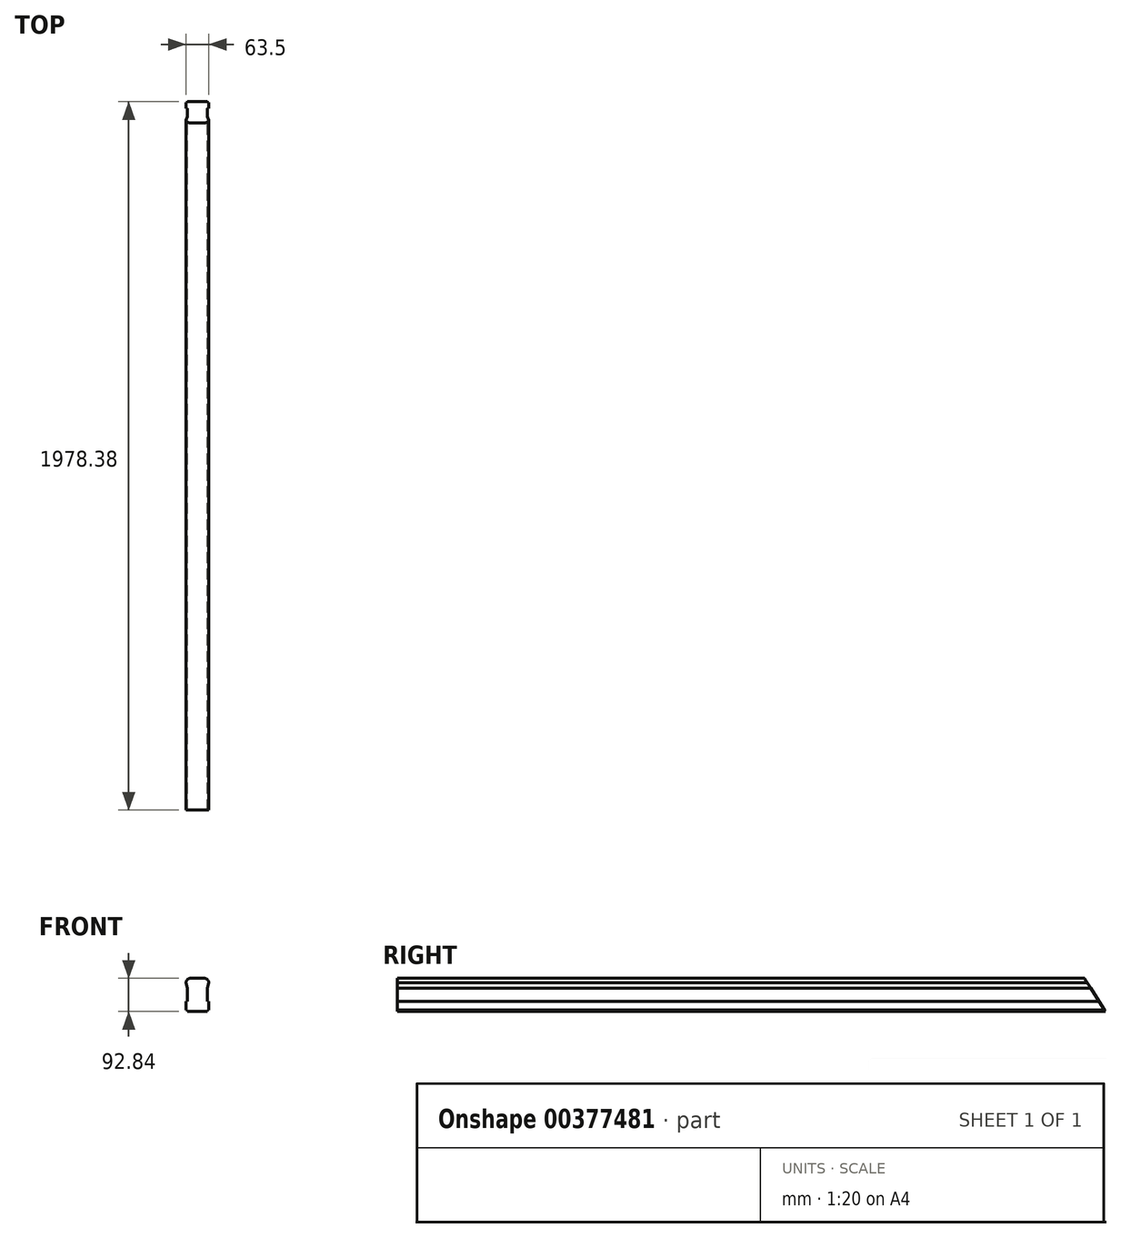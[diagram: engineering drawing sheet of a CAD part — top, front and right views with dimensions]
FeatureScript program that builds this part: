
annotation { "Feature Type Name" : "Feature", "Feature Type Description" : "" }
export const myFeature = defineFeature(function(context is Context, id is Id, definition is map)
    precondition{}
    {
        {
            var Q0;
            Q0=qCreatedBy(makeId("Front.planeOp"),FACE);
            var sketch = newSketch(context, id + "F0", { "sketchPlane" : qUnion([Q0])});
            skLineSegment(sketch, "E0.bottom", {"start": v(-19.05, 44.45) * mm, "end": v(19.05, 44.45) * mm});
            skLineSegment(sketch, "E0.top", {"start": v(-31.75, -44.45) * mm, "end": v(-27.75, -44.45) * mm});
            skLineSegment(sketch, "E0.left", {"start": v(-31.75, -20.19) * mm, "end": v(-31.75, -44.45) * mm});
            skLineSegment(sketch, "E0.right", {"start": v(31.75, -20.19) * mm, "end": v(31.75, -44.45) * mm});
            skPoint(sketch, "E0.middle", {"position": v(0, 0) * mm});
            skPoint(sketch, "E1.visualSharp", {"position": v(-31.75, 44.45) * mm});
            skArc(sketch, "E1.filletArc", {"start": v(-19.05, 44.45) * mm, "mid": v(-28.03, 40.73) * mm, "end": v(-31.75, 31.75) * mm});
            skPoint(sketch, "E2.visualSharp", {"position": v(31.75, 44.45) * mm});
            skArc(sketch, "E2.filletArc", {"start": v(31.75, 31.75) * mm, "mid": v(28.03, 40.73) * mm, "end": v(19.05, 44.45) * mm});
            skLineSegment(sketch, "E3.top", {"start": v(-27.75, -48.39) * mm, "end": v(27.75, -48.39) * mm});
            skLineSegment(sketch, "E3.left", {"start": v(-27.75, 16.4) * mm, "end": v(-27.75, -20.19) * mm});
            skLineSegment(sketch, "E3.right", {"start": v(27.75, 16.4) * mm, "end": v(27.75, -20.19) * mm});
            skPoint(sketch, "E3.middle", {"position": v(0, -16) * mm});
            skLineSegment(sketch, "E4", {"start": v(-31.75, 31.75) * mm, "end": v(-27.75, 16.4) * mm});
            skLineSegment(sketch, "E5", {"start": v(31.75, 31.75) * mm, "end": v(27.75, 16.4) * mm});
            skLineSegment(sketch, "E6", {"start": v(-27.75, -20.19) * mm, "end": v(-31.75, -20.19) * mm});
            skPoint(sketch, "E6.endSnap0", {"position": v(-31.75, -6.35) * mm});
            skLineSegment(sketch, "E7", {"start": v(27.75, -20.19) * mm, "end": v(31.75, -20.19) * mm});
            skLineSegment(sketch, "E8.trimOffspring", {"start": v(27.75, -44.45) * mm, "end": v(27.75, -48.39) * mm});
            skLineSegment(sketch, "E9.trimOffspring", {"start": v(-27.75, -44.45) * mm, "end": v(-27.75, -48.39) * mm});
            skLineSegment(sketch, "E10.trimOffspring", {"start": v(27.75, -44.45) * mm, "end": v(31.75, -44.45) * mm});
            skSolve(sketch);
        }
        {
            var Q0;
            Q0 = qSketchRegion(id + "F0", true);
            extrude(context, id + "F1", {"entities" : qUnion([Q0]), "depth" : 1981.2 * mm, "offsetDistance" : 25.4 * mm});
        }
        {
            var Q0;
            Q0=qCreatedBy(makeId("Right.planeOp"),FACE);
            var sketch = newSketch(context, id + "F2", { "sketchPlane" : qUnion([Q0])});
            skLineSegment(sketch, "E11", {"start": v(0, -52.82) * mm, "end": v(-108.47, 117.63) * mm});
            skLineSegment(sketch, "E12", {"start": v(-108.47, 117.63) * mm, "end": v(0, 117.63) * mm});
            skLineSegment(sketch, "E13", {"start": v(0, 117.63) * mm, "end": v(0, -52.82) * mm});
            skSolve(sketch);
        }
        {
            var Q0;
            Q0 = qSketchRegion(id + "F2", true);
            extrude(context, id + "F3", {"entities" : qUnion([Q0]), "operationType" : NewBodyOperationType.REMOVE, "oppositeDirection" : true, "depth" : 50.8 * mm, "offsetDistance" : 25.4 * mm, "hasSecondDirection" : true, "secondDirectionOppositeDirection" : false, "secondDirectionDepth" : 50.8 * mm});
        }
    });
